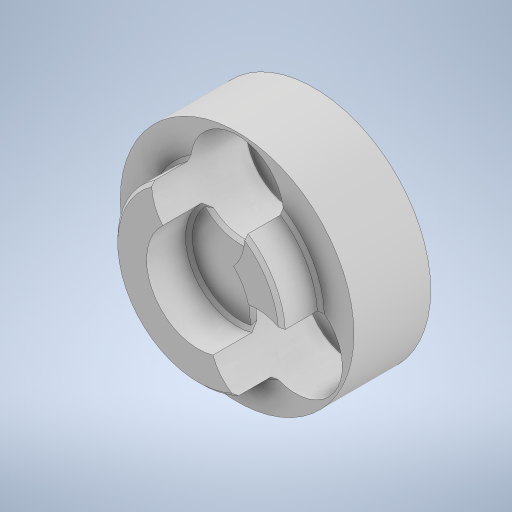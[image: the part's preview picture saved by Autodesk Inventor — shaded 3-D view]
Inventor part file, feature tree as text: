
AUTODESK INVENTOR PART (.ipt)
format: ipt  version: 2023 (Build 270158000, 158)  size: 337,408 bytes
history: native  units: mm
features: extrude x4, chamfer x4, sketch x4
ambient origin geometry x8: Origin, YZ Plane, XZ Plane, XY Plane, X Axis, Y Axis, Z Axis, Center Point
bodies: Solid1 (feature_tree)
feature tree (12):
  extrude  "Extrusion1"  Depth=8.0mm
  extrude  "Extrusion2"  Depth=30.0mm TaperAngle=360.0deg
  extrude  "Extrusion3"  Depth=4.53mm
  extrude  "Extrusion4"  Depth=6.1mm
  chamfer  "Chamfer1"  Distance=2.5mm
  chamfer  "Chamfer2"  Distance=5.5mm
  chamfer  "Chamfer3"  Distance=30.0mm Angle=360.0deg
  chamfer  "Chamfer4"  Distance=5.6mm
  sketch  "Sketch1"  dims[d0=13.8mm d1=8.0mm]
  sketch  "Sketch2"  dims[d2=3.0mm d3=30.0mm d5=360.0deg]
  sketch  "Sketch3"  dims[d7=4.53mm d8=0.0mm d9=9.9mm]
  sketch  "Sketch4"  dims[d10=2.3mm d11=0.0mm d12=6.1mm d13=2.5mm d14=0.0mm d15=5.5mm d16=30.0mm d18=360.0deg d20=5.6mm d21=0.0mm d22=0.2mm d23=2.0mm d24=45.0deg d25=0.2mm d26=2.0mm d27=45.0deg d28=0.2mm d29=2.0mm d30=45.0deg d31=0.2mm d32=2.0mm d33=45.0deg]
